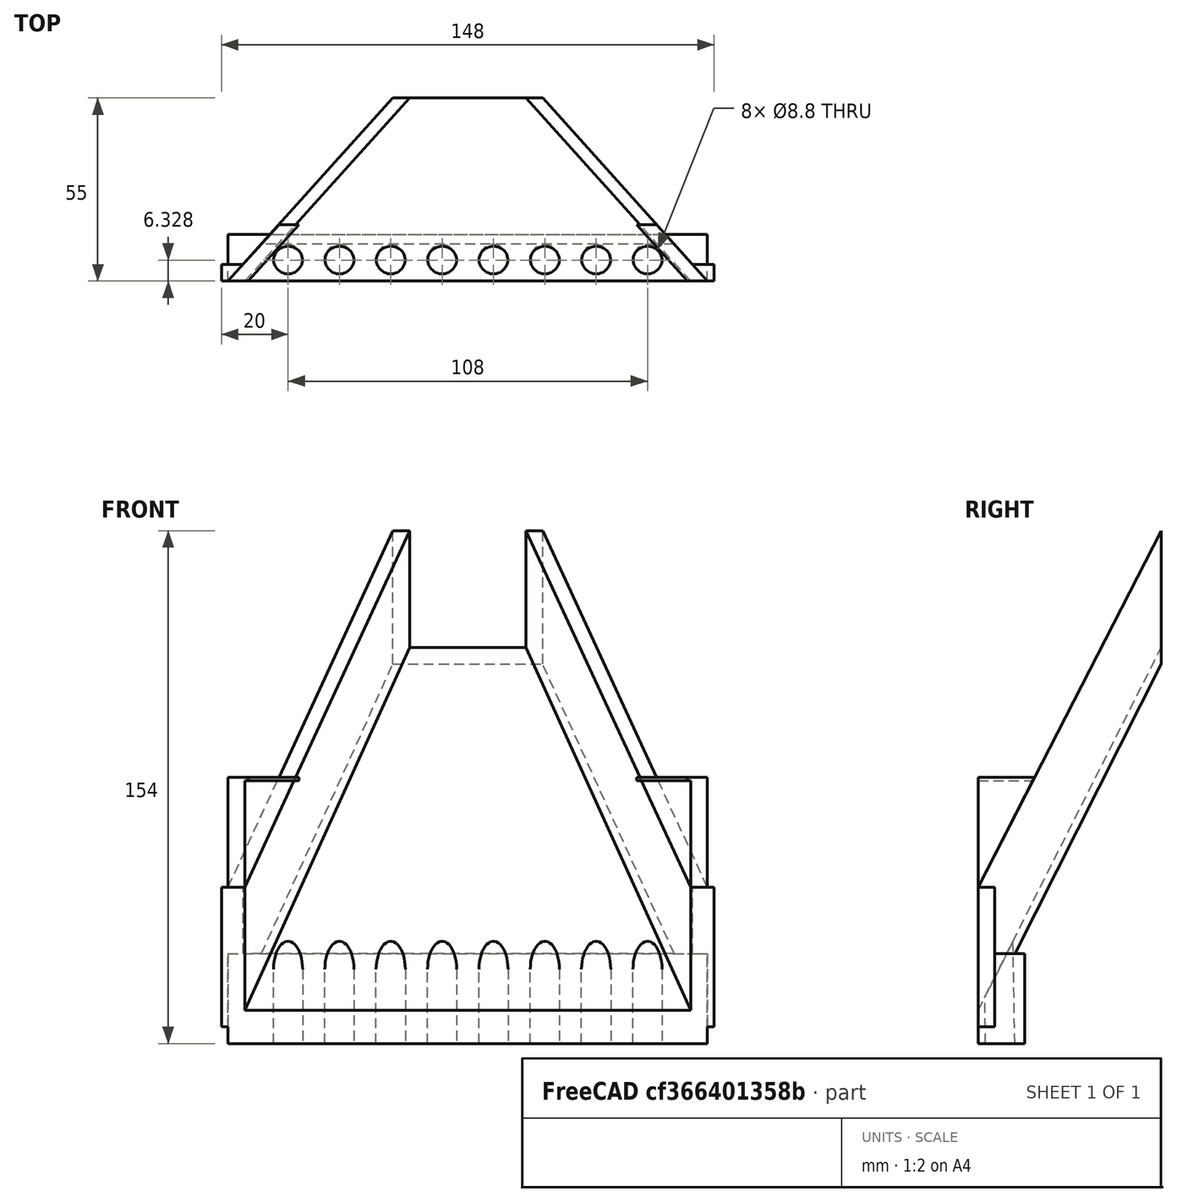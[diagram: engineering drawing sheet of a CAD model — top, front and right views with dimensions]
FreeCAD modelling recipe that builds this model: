
FCSTD DOCUMENT  (FreeCAD 0.20R29603 (Git))
Label: trichter_Ausgang4
License: All rights reserved
LicenseURL: http://en.wikipedia.org/wiki/All_rights_reserved
objects: TechDraw::DrawViewDimension×24, TechDraw::DrawProjGroupItem×9, PartDesign::AdditiveWedge×5, PartDesign::Body×3, TechDraw::DrawSVGTemplate×2, PartDesign::AdditiveBox×2, TechDraw::DrawPage×2, TechDraw::DrawProjGroup×2, PartDesign::SubtractiveWedge×1, PartDesign::SubtractiveCylinder×1, PartDesign::LinearPattern×1, TechDraw::DrawViewDetail×1
note: 22 computed .brp shape members not serialized (recipe doc carries the construction recipe); baked Part::Feature solids carry a one-line shape summary decoded from their .brp

FEATURE [TechDraw::DrawSVGTemplate] Template001
  EditableTexts = Designed_by_Name=B.Schulze; Drawing_number=1; FC-Date=11.08.2023; FC-SC=Scale; FC-SH=6; FC-Title=Eisdosierer; Subtitle=Trichter Ausgang
  Height = 210
  Orientation = 1
  Width = 297
FEATURE [TechDraw::DrawSVGTemplate] Template
  EditableTexts = Designed_by_Name=B. Schulze; Drawing_number=1; FC-Date=13.09.2023; FC-SC=1:1; FC-SH=7; FC-Title=Eisdosierer; Subtitle=Trichter Ausgang Seiten
  Height = 210
  Orientation = 1
  Width = 297
FEATURE [PartDesign::Body] Body
  Group = -> [Wedge,Box,Box001,Wedge001,Cylinder,LinearPattern]
  Origin = -> Origin
  Tip = -> LinearPattern
FEATURE [PartDesign::AdditiveWedge] Wedge
  AttacherType = Attacher::AttachEngine3D
  MapMode = 2
  Support = -> [Body]
  X2max = 94.5
  X2min = 49.5
  Xmax = 144
  Xmin = 0
  Ymax = 55
  Ymin = 0
  Z2max = 149
  Z2min = 109
  Zmax = 42
  Zmin = 0
FEATURE [PartDesign::AdditiveBox] Box
  AttacherType = Attacher::AttachEngine3D
  AttachmentOffset = pos=(-2,0,0) rot=(0,0,1;0rad)
  BaseFeature = -> Wedge
  Height = 42
  Length = 148
  MapMode = 2
  Placement = pos=(-2,0,0) rot=(0,0,1;0rad)
  Support = -> [Body]
  Width = 5
FEATURE [PartDesign::AdditiveBox] Box001
  AttacherType = Attacher::AttachEngine3D
  AttachmentOffset = pos=(0,0,-5) rot=(0,0,1;0rad)
  BaseFeature = -> Box
  Height = 27
  Length = 144
  MapMode = 2
  Placement = pos=(0,0,-5) rot=(0,0,1;0rad)
  Support = -> [Body]
  Width = 14
FEATURE [PartDesign::SubtractiveWedge] Wedge001
  AttacherType = Attacher::AttachEngine3D
  BaseFeature = -> Box001
  MapMode = 2
  Support = -> [Body]
  X2max = 89.5
  X2min = 54.5
  Xmax = 139
  Xmin = 5
  Ymax = 55
  Ymin = 0
  Z2max = 149
  Z2min = 114
  Zmax = 42
  Zmin = 5
FEATURE [PartDesign::SubtractiveCylinder] Cylinder
  Angle = 360
  AttacherType = Attacher::AttachEngine3D
  AttachmentOffset = pos=(18,-6,-34) rot=(1,0,0;0.017453rad)
  BaseFeature = -> Wedge001
  FirstAngle = 0
  Height = 35
  MapMode = 5
  Placement = pos=(18,6,29) rot=(1,0,0;3.15905rad)
  Radius = 4.4
  SecondAngle = 0
  Support = -> [Box001]
FEATURE [PartDesign::LinearPattern] LinearPattern
  BaseFeature = -> Cylinder
  Direction = -> X_Axis
  Length = 108
  Occurrences = 8
  Originals = -> [Cylinder]
  Placement = pos=(18,6,29) rot=(1,0,0;3.15905rad)
FEATURE [TechDraw::DrawPage] Page001
  KeepUpdated = true
  NextBalloonIndex = 1
  ProjectionType = 0
  Template = -> Template001
  Views = -> [ProjGroup,Detail,Dimension,Dimension001,Dimension002,Dimension003,Dimension004,Dimension005,Dimension006,Dimension007,Dimension008,Dimension009,Dimension010,Dimension011,Dimension012,Dimension013,Dimension014,Dimension015]
FEATURE [TechDraw::DrawProjGroup] ProjGroup
  Anchor = -> ProjItem
  AutoDistribute = false
  LockPosition = false
  ProjectionType = 0
  Rotation = 0
  Scale = 0.333333
  ScaleType = 2
  Source = -> [Body]
  Views = -> [ProjItem,ProjItem001,ProjItem002,ProjItem003,ProjItem004,ProjItem005,ProjItem006]
  X = 116.869
  Y = 105.822
  spacingX = 15
  spacingY = 15
FEATURE [TechDraw::DrawProjGroupItem] ProjItem  label="Front"
  CoarseView = false
  Direction = (-3e-16,0,1)
  Focus = 100
  HardHidden = false
  IsoCount = 0
  IsoHidden = false
  IsoVisible = false
  LockPosition = true
  Perspective = false
  Rotation = 0
  RotationVector = (0,0,1)
  Scale = 0.333333
  ScaleType = 2
  SeamHidden = false
  SeamVisible = true
  SmoothHidden = false
  SmoothVisible = true
  Source = -> [Body]
  Type = 0
  X = 0
  XDirection = (-1,0,-3e-16)
  Y = 0
FEATURE [TechDraw::DrawProjGroupItem] ProjItem001  label="Bottom"
  CoarseView = false
  Direction = (0,1,0)
  Focus = 100
  HardHidden = false
  IsoCount = 0
  IsoHidden = false
  IsoVisible = false
  LockPosition = false
  Perspective = false
  Rotation = 0
  RotationVector = (1,0,0)
  Scale = 0.333333
  ScaleType = 2
  SeamHidden = false
  SeamVisible = true
  SmoothHidden = false
  SmoothVisible = true
  Source = -> [Body]
  Type = 5
  X = 0
  XDirection = (-1,0,-3e-16)
  Y = 55.5717
FEATURE [TechDraw::DrawProjGroupItem] ProjItem002  label="FrontBottomLeft"
  CoarseView = false
  Direction = (0.57735,0.57735,0.57735)
  Focus = 100
  HardHidden = false
  IsoCount = 0
  IsoHidden = false
  IsoVisible = false
  LockPosition = false
  Perspective = false
  Rotation = 0
  RotationVector = (1,0,0)
  Scale = 0.333333
  ScaleType = 2
  SeamHidden = false
  SeamVisible = true
  SmoothHidden = false
  SmoothVisible = true
  Source = -> [Body]
  Type = 8
  X = 71.7719
  XDirection = (-0.707107,0,0.707107)
  Y = 57.8217
FEATURE [TechDraw::DrawProjGroupItem] ProjItem003  label="Top"
  CoarseView = false
  Direction = (0,-1,0)
  Focus = 100
  HardHidden = false
  IsoCount = 0
  IsoHidden = false
  IsoVisible = false
  LockPosition = false
  Perspective = false
  Rotation = 0
  RotationVector = (1,0,0)
  Scale = 0.333333
  ScaleType = 2
  SeamHidden = false
  SeamVisible = true
  SmoothHidden = false
  SmoothVisible = true
  Source = -> [Body]
  Type = 4
  X = 0
  XDirection = (-1,0,-3e-16)
  Y = -60.5218
FEATURE [TechDraw::DrawProjGroupItem] ProjItem004  label="Left"
  CoarseView = false
  Direction = (1,0,4e-16)
  Focus = 100
  HardHidden = false
  IsoCount = 0
  IsoHidden = false
  IsoVisible = false
  LockPosition = false
  Perspective = false
  Rotation = 0
  RotationVector = (1,0,0)
  Scale = 0.333333
  ScaleType = 2
  SeamHidden = false
  SeamVisible = true
  SmoothHidden = false
  SmoothVisible = true
  Source = -> [Body]
  Type = 1
  X = 73.572
  XDirection = (-4e-16,0,1)
  Y = 0
FEATURE [TechDraw::DrawProjGroupItem] ProjItem005  label="Right"
  CoarseView = false
  Direction = (-1,0,-2e-16)
  Focus = 100
  HardHidden = false
  IsoCount = 0
  IsoHidden = false
  IsoVisible = false
  LockPosition = false
  Perspective = false
  Rotation = 0
  RotationVector = (1,0,0)
  Scale = 0.333333
  ScaleType = 2
  SeamHidden = false
  SeamVisible = true
  SmoothHidden = false
  SmoothVisible = true
  Source = -> [Body]
  Type = 2
  X = -73.572
  XDirection = (2e-16,0,-1)
  Y = 0
FEATURE [TechDraw::DrawProjGroupItem] ProjItem006  label="Rear"
  CoarseView = false
  Direction = (3e-16,0,-1)
  Focus = 100
  HardHidden = false
  IsoCount = 0
  IsoHidden = false
  IsoVisible = false
  LockPosition = false
  Perspective = false
  Rotation = 0
  RotationVector = (1,0,0)
  Scale = 0.333333
  ScaleType = 2
  SeamHidden = false
  SeamVisible = true
  SmoothHidden = false
  SmoothVisible = true
  Source = -> [Body]
  Type = 3
  X = 135.894
  XDirection = (1,0,3e-16)
  Y = 0
FEATURE [TechDraw::DrawViewDetail] Detail
  AnchorPoint = (-53.15,20.74,0)
  BaseView = -> ProjItem006
  Caption = Schlauchbohrung
  CoarseView = false
  Direction = (3e-16,0,-1)
  Focus = 100
  HardHidden = false
  IsoCount = 0
  IsoHidden = false
  IsoVisible = false
  LockPosition = false
  Perspective = false
  Radius = 6
  Reference = 1
  Rotation = 0
  Scale = 2
  ScaleType = 2
  SeamHidden = false
  SeamVisible = true
  SmoothHidden = false
  SmoothVisible = true
  Source = -> [Body]
  X = 245.614
  XDirection = (1,0,3e-16)
  Y = 175.252
FEATURE [TechDraw::DrawViewDimension] Dimension
  AngleOverride = false
  Arbitrary = false
  ArbitraryTolerances = false
  EqualTolerance = true
  ExtensionAngle = 0
  FormatSpec = %.2w
  FormatSpecOverTolerance = %+.2w
  FormatSpecUnderTolerance = %+.2w
  Inverted = false
  LineAngle = 0
  LockPosition = false
  MeasureType = 1
  OverTolerance = 0
  References2D = -> [Detail]
  Rotation = 0
  ScaleType = 0
  TheoreticalExact = false
  Type = 1
  UnderTolerance = 0
  X = -0.438518
  Y = 22.5625
FEATURE [TechDraw::DrawViewDimension] Dimension001
  AngleOverride = false
  Arbitrary = false
  ArbitraryTolerances = false
  EqualTolerance = true
  ExtensionAngle = 0
  FormatSpec = %.2w
  FormatSpecOverTolerance = %+.2w
  FormatSpecUnderTolerance = %+.2w
  Inverted = false
  LineAngle = 0
  LockPosition = false
  MeasureType = 1
  OverTolerance = 0
  References2D = -> [ProjItem001]
  Rotation = 0
  ScaleType = 0
  TheoreticalExact = false
  Type = 1
  UnderTolerance = 0
  X = -1.3369
  Y = 36.2931
FEATURE [TechDraw::DrawViewDimension] Dimension002
  AngleOverride = false
  Arbitrary = false
  ArbitraryTolerances = false
  EqualTolerance = true
  ExtensionAngle = 0
  FormatSpec = %.2w
  FormatSpecOverTolerance = %+.2w
  FormatSpecUnderTolerance = %+.2w
  Inverted = false
  LineAngle = 0
  LockPosition = false
  MeasureType = 1
  OverTolerance = 0
  References2D = -> [ProjItem001]
  Rotation = 0
  ScaleType = 0
  TheoreticalExact = false
  Type = 1
  UnderTolerance = 0
  X = 0.121131
  Y = 22.0827
FEATURE [TechDraw::DrawViewDimension] Dimension003
  AngleOverride = false
  Arbitrary = false
  ArbitraryTolerances = false
  EqualTolerance = true
  ExtensionAngle = 0
  FormatSpec = %.2w
  FormatSpecOverTolerance = %+.2w
  FormatSpecUnderTolerance = %+.2w
  Inverted = false
  LineAngle = 0
  LockPosition = false
  MeasureType = 1
  OverTolerance = 0
  References2D = -> [ProjItem001]
  Rotation = 0
  ScaleType = 0
  TheoreticalExact = false
  Type = 2
  UnderTolerance = 0
  X = -23.8213
  Y = 22.4046
FEATURE [TechDraw::DrawViewDimension] Dimension004
  AngleOverride = false
  Arbitrary = false
  ArbitraryTolerances = false
  EqualTolerance = true
  ExtensionAngle = 0
  FormatSpec = %.2w
  FormatSpecOverTolerance = %+.2w
  FormatSpecUnderTolerance = %+.2w
  Inverted = false
  LineAngle = 0
  LockPosition = false
  MeasureType = 1
  OverTolerance = 0
  References2D = -> [ProjItem001]
  Rotation = 0
  ScaleType = 0
  TheoreticalExact = false
  Type = 2
  UnderTolerance = 0
  X = 20.0194
  Y = 19.9974
FEATURE [TechDraw::DrawViewDimension] Dimension005
  AngleOverride = false
  Arbitrary = false
  ArbitraryTolerances = false
  EqualTolerance = true
  ExtensionAngle = 0
  FormatSpec = %.2w
  FormatSpecOverTolerance = %+.2w
  FormatSpecUnderTolerance = %+.2w
  Inverted = false
  LineAngle = 0
  LockPosition = false
  MeasureType = 1
  OverTolerance = 0
  References2D = -> [ProjItem004]
  Rotation = 0
  ScaleType = 0
  TheoreticalExact = false
  Type = 1
  UnderTolerance = 0
  X = -21.4466
  Y = -3.72737
FEATURE [TechDraw::DrawViewDimension] Dimension006
  AngleOverride = false
  Arbitrary = false
  ArbitraryTolerances = false
  EqualTolerance = true
  ExtensionAngle = 0
  FormatSpec = %.2w
  FormatSpecOverTolerance = %+.2w
  FormatSpecUnderTolerance = %+.2w
  Inverted = false
  LineAngle = 0
  LockPosition = false
  MeasureType = 1
  OverTolerance = 0
  References2D = -> [ProjItem004]
  Rotation = 0
  ScaleType = 0
  TheoreticalExact = false
  Type = 0
  UnderTolerance = 0
  X = -2.59202
  Y = -2.62069
FEATURE [TechDraw::DrawViewDimension] Dimension007
  AngleOverride = false
  Arbitrary = false
  ArbitraryTolerances = false
  EqualTolerance = true
  ExtensionAngle = 0
  FormatSpec = %.2w
  FormatSpecOverTolerance = %+.2w
  FormatSpecUnderTolerance = %+.2w
  Inverted = false
  LineAngle = 0
  LockPosition = false
  MeasureType = 1
  OverTolerance = 0
  References2D = -> [ProjItem004]
  Rotation = 0
  ScaleType = 0
  TheoreticalExact = false
  Type = 0
  UnderTolerance = 0
  X = 14.6032
  Y = 9.18643
FEATURE [TechDraw::DrawViewDimension] Dimension008
  AngleOverride = false
  Arbitrary = false
  ArbitraryTolerances = false
  EqualTolerance = true
  ExtensionAngle = 0
  FormatSpec = %.2w
  FormatSpecOverTolerance = %+.2w
  FormatSpecUnderTolerance = %+.2w
  Inverted = false
  LineAngle = 0
  LockPosition = false
  MeasureType = 1
  OverTolerance = 0
  References2D = -> [ProjItem004]
  Rotation = 0
  ScaleType = 0
  TheoreticalExact = false
  Type = 2
  UnderTolerance = 0
  X = -37.081
  Y = 9.24611
FEATURE [TechDraw::DrawViewDimension] Dimension009
  AngleOverride = false
  Arbitrary = false
  ArbitraryTolerances = false
  EqualTolerance = true
  ExtensionAngle = 0
  FormatSpec = %.2w
  FormatSpecOverTolerance = %+.2w
  FormatSpecUnderTolerance = %+.2w
  Inverted = false
  LineAngle = 0
  LockPosition = false
  MeasureType = 1
  OverTolerance = 0
  References2D = -> [ProjItem004]
  Rotation = 0
  ScaleType = 0
  TheoreticalExact = false
  Type = 1
  UnderTolerance = 0
  X = -16.3864
  Y = 21.9147
FEATURE [TechDraw::DrawViewDimension] Dimension010
  AngleOverride = false
  Arbitrary = false
  ArbitraryTolerances = false
  EqualTolerance = true
  ExtensionAngle = 0
  FormatSpec = %.2w
  FormatSpecOverTolerance = %+.2w
  FormatSpecUnderTolerance = %+.2w
  Inverted = false
  LineAngle = 0
  LockPosition = false
  MeasureType = 1
  OverTolerance = 0
  References2D = -> [ProjItem005]
  Rotation = 0
  ScaleType = 0
  TheoreticalExact = false
  Type = 2
  UnderTolerance = 0
  X = -1.01314
  Y = 11.2756
FEATURE [TechDraw::DrawViewDimension] Dimension011
  AngleOverride = false
  Arbitrary = false
  ArbitraryTolerances = false
  EqualTolerance = true
  ExtensionAngle = 0
  FormatSpec = %.2w
  FormatSpecOverTolerance = %+.2w
  FormatSpecUnderTolerance = %+.2w
  Inverted = false
  LineAngle = 0
  LockPosition = false
  MeasureType = 1
  OverTolerance = 0
  References2D = -> [ProjItem003]
  Rotation = 0
  ScaleType = 0
  TheoreticalExact = false
  Type = 1
  UnderTolerance = 0
  X = 0.229292
  Y = 39.3296
FEATURE [TechDraw::DrawViewDimension] Dimension012
  AngleOverride = false
  Arbitrary = false
  ArbitraryTolerances = false
  EqualTolerance = true
  ExtensionAngle = 0
  FormatSpec = %.2w
  FormatSpecOverTolerance = %+.2w
  FormatSpecUnderTolerance = %+.2w
  Inverted = false
  LineAngle = 0
  LockPosition = false
  MeasureType = 1
  OverTolerance = 0
  References2D = -> [ProjItem003]
  Rotation = 0
  ScaleType = 0
  TheoreticalExact = false
  Type = 1
  UnderTolerance = 0
  X = -32.0146
  Y = 2.51505
FEATURE [TechDraw::DrawViewDimension] Dimension013
  AngleOverride = false
  Arbitrary = false
  ArbitraryTolerances = false
  EqualTolerance = true
  ExtensionAngle = 0
  FormatSpec = %.2w
  FormatSpecOverTolerance = %+.2w
  FormatSpecUnderTolerance = %+.2w
  Inverted = false
  LineAngle = 0
  LockPosition = false
  MeasureType = 1
  OverTolerance = 0
  References2D = -> [ProjItem003]
  Rotation = 0
  ScaleType = 0
  TheoreticalExact = false
  Type = 2
  UnderTolerance = 0
  X = 30.6495
  Y = 29.6155
FEATURE [TechDraw::DrawViewDimension] Dimension014
  AngleOverride = false
  Arbitrary = false
  ArbitraryTolerances = false
  EqualTolerance = true
  ExtensionAngle = 0
  FormatSpec = %.2w
  FormatSpecOverTolerance = %+.2w
  FormatSpecUnderTolerance = %+.2w
  Inverted = false
  LineAngle = 0
  LockPosition = false
  MeasureType = 1
  OverTolerance = 0
  References2D = -> [ProjItem006]
  Rotation = 0
  ScaleType = 0
  TheoreticalExact = false
  Type = 1
  UnderTolerance = 0
  X = -29.2699
  Y = 19.6135
FEATURE [TechDraw::DrawViewDimension] Dimension015
  AngleOverride = false
  Arbitrary = false
  ArbitraryTolerances = false
  EqualTolerance = true
  ExtensionAngle = 0
  FormatSpec = %.2w
  FormatSpecOverTolerance = %+.2w
  FormatSpecUnderTolerance = %+.2w
  Inverted = false
  LineAngle = 0
  LockPosition = false
  MeasureType = 1
  OverTolerance = 0
  References2D = -> [ProjItem006]
  Rotation = 0
  ScaleType = 0
  TheoreticalExact = false
  Type = 1
  UnderTolerance = 0
  X = 0.949326
  Y = 16.3942
FEATURE [PartDesign::Body] Body001  label="Seite1"
  Group = -> [Wedge002,Wedge005]
  Origin = -> Origin001
  Tip = -> Wedge005
FEATURE [PartDesign::AdditiveWedge] Wedge002
  AttacherType = Attacher::AttachEngine3D
  AttachmentOffset = pos=(0,0,42) rot=(0,0,1;0rad)
  MapMode = 2
  Placement = pos=(0,0,42) rot=(0,0,1;0rad)
  Support = -> [Body]
  X2max = 20.27
  X2min = 15.27
  Xmax = 5
  Xmin = 0
  Ymax = 16.96
  Ymin = 0
  Z2max = 33
  Z2min = 33
  Zmax = 33
  Zmin = 0
FEATURE [PartDesign::Body] Body002  label="Seite2"
  Group = -> [Wedge003,Wedge004]
  Origin = -> Origin002
  Tip = -> Wedge004
FEATURE [PartDesign::AdditiveWedge] Wedge003
  AttacherType = Attacher::AttachEngine3D
  AttachmentOffset = pos=(123.73,0,42) rot=(0,0,1;0rad)
  MapMode = 2
  Placement = pos=(123.73,0,42) rot=(0,0,1;0rad)
  Support = -> [Body]
  X2max = 5
  X2min = 0
  Xmax = 20.27
  Xmin = 15.27
  Ymax = 16.96
  Ymin = 0
  Z2max = 33
  Z2min = 33
  Zmax = 33
  Zmin = 0
FEATURE [PartDesign::AdditiveWedge] Wedge004
  AttacherType = Attacher::AttachEngine3D
  AttachmentOffset = pos=(122.73,0,74) rot=(0,0,1;0rad)
  BaseFeature = -> Wedge003
  MapMode = 2
  Placement = pos=(122.73,0,74) rot=(0,0,1;0rad)
  Support = -> [Body]
  X2max = 1
  X2min = 0
  Xmax = 16.27
  Xmin = 15.27
  Ymax = 16.96
  Ymin = 0
  Z2max = 1
  Z2min = 0
  Zmax = 1
  Zmin = 0
FEATURE [PartDesign::AdditiveWedge] Wedge005
  AttacherType = Attacher::AttachEngine3D
  AttachmentOffset = pos=(5,0,74) rot=(0,0,1;0rad)
  BaseFeature = -> Wedge002
  MapMode = 2
  Placement = pos=(5,0,74) rot=(0,0,1;0rad)
  Support = -> [Body]
  X2max = 16.27
  X2min = 15.27
  Xmax = 1
  Xmin = 0
  Ymax = 16.96
  Ymin = 0
  Z2max = 1
  Z2min = 0
  Zmax = 1
  Zmin = 0
FEATURE [TechDraw::DrawPage] Page
  KeepUpdated = true
  NextBalloonIndex = 1
  ProjectionType = 0
  Template = -> Template
  Views = -> [ProjGroup001,Dimension016,Dimension017,Dimension018,Dimension019,Dimension020,Dimension021,Dimension022,Dimension023]
FEATURE [TechDraw::DrawProjGroup] ProjGroup001
  Anchor = -> ProjItem007
  AutoDistribute = true
  LockPosition = false
  ProjectionType = 0
  Rotation = 0
  ScaleType = 0
  Source = -> [Body002]
  Views = -> [ProjItem007,ProjItem009]
  X = 62.6533
  Y = 151.174
  spacingX = 15
  spacingY = 15
FEATURE [TechDraw::DrawProjGroupItem] ProjItem007  label="Front001"
  CoarseView = false
  Direction = (0,-1,0)
  Focus = 100
  HardHidden = false
  IsoCount = 0
  IsoHidden = false
  IsoVisible = false
  LockPosition = true
  Perspective = false
  Rotation = 0
  RotationVector = (-1,0,0)
  ScaleType = 2
  SeamHidden = false
  SeamVisible = true
  SmoothHidden = false
  SmoothVisible = true
  Source = -> [Body002]
  Type = 0
  X = 0
  XDirection = (3e-16,0,1)
  Y = 0
FEATURE [TechDraw::DrawViewDimension] Dimension016
  AngleOverride = false
  Arbitrary = false
  ArbitraryTolerances = false
  EqualTolerance = true
  ExtensionAngle = 0
  FormatSpec = %.2w
  FormatSpecOverTolerance = %+.2w
  FormatSpecUnderTolerance = %+.2w
  Inverted = false
  LineAngle = 0
  LockPosition = false
  MeasureType = 1
  OverTolerance = 0
  References2D = -> [ProjItem007]
  Rotation = 0
  ScaleType = 0
  TheoreticalExact = false
  Type = 1
  UnderTolerance = 0
  X = 4.32374
  Y = -28.1814
FEATURE [TechDraw::DrawViewDimension] Dimension017
  AngleOverride = false
  Arbitrary = false
  ArbitraryTolerances = false
  EqualTolerance = true
  ExtensionAngle = 0
  FormatSpec = %.2w
  FormatSpecOverTolerance = %+.2w
  FormatSpecUnderTolerance = %+.2w
  Inverted = false
  LineAngle = 0
  LockPosition = false
  MeasureType = 1
  OverTolerance = 0
  References2D = -> [ProjItem007]
  Rotation = 0
  ScaleType = 0
  TheoreticalExact = false
  Type = 0
  UnderTolerance = 0
  X = -9.87309
  Y = 16.3095
FEATURE [TechDraw::DrawViewDimension] Dimension018
  AngleOverride = false
  Arbitrary = false
  ArbitraryTolerances = false
  EqualTolerance = true
  ExtensionAngle = 0
  FormatSpec = %.2w
  FormatSpecOverTolerance = %+.2w
  FormatSpecUnderTolerance = %+.2w
  Inverted = false
  LineAngle = 0
  LockPosition = false
  MeasureType = 1
  OverTolerance = 0
  References2D = -> [ProjItem007]
  Rotation = 0
  ScaleType = 0
  TheoreticalExact = false
  Type = 2
  UnderTolerance = 0
  X = -31.1364
  Y = -4.55349
FEATURE [TechDraw::DrawViewDimension] Dimension019
  AngleOverride = false
  Arbitrary = false
  ArbitraryTolerances = false
  EqualTolerance = true
  ExtensionAngle = 0
  FormatSpec = %.2w
  FormatSpecOverTolerance = %+.2w
  FormatSpecUnderTolerance = %+.2w
  Inverted = false
  LineAngle = 0
  LockPosition = false
  MeasureType = 1
  OverTolerance = 0
  References2D = -> [ProjItem007]
  Rotation = 0
  ScaleType = 0
  TheoreticalExact = false
  Type = 1
  UnderTolerance = 0
  X = 17.8689
  Y = 28.335
FEATURE [TechDraw::DrawViewDimension] Dimension020
  AngleOverride = false
  Arbitrary = false
  ArbitraryTolerances = false
  EqualTolerance = true
  ExtensionAngle = 0
  FormatSpec = %.2w
  FormatSpecOverTolerance = %+.2w
  FormatSpecUnderTolerance = %+.2w
  Inverted = false
  LineAngle = 0
  LockPosition = false
  MeasureType = 1
  OverTolerance = 0
  References2D = -> [ProjItem007]
  Rotation = 0
  ScaleType = 0
  TheoreticalExact = false
  Type = 2
  UnderTolerance = 0
  X = 23.2293
  Y = 4.26788
FEATURE [TechDraw::DrawViewDimension] Dimension021
  AngleOverride = false
  Arbitrary = false
  ArbitraryTolerances = false
  EqualTolerance = true
  ExtensionAngle = 0
  FormatSpec = %.2w
  FormatSpecOverTolerance = %+.2w
  FormatSpecUnderTolerance = %+.2w
  Inverted = false
  LineAngle = 0
  LockPosition = false
  MeasureType = 1
  OverTolerance = 0
  References2D = -> [ProjItem007]
  Rotation = 0
  ScaleType = 0
  TheoreticalExact = false
  Type = 2
  UnderTolerance = 0
  X = 28.916
  Y = -4.53058
FEATURE [TechDraw::DrawProjGroupItem] ProjItem009  label="Left001"
  CoarseView = false
  Direction = (-3e-16,-1e-16,-1)
  Focus = 100
  HardHidden = false
  IsoCount = 0
  IsoHidden = false
  IsoVisible = false
  LockPosition = false
  Perspective = false
  Rotation = 0
  RotationVector = (1,0,0)
  ScaleType = 2
  SeamHidden = false
  SeamVisible = true
  SmoothHidden = false
  SmoothVisible = true
  Source = -> [Body002]
  Type = 1
  X = 88.1786
  XDirection = (0,-1,1e-16)
  Y = 0
FEATURE [TechDraw::DrawViewDimension] Dimension022
  AngleOverride = false
  Arbitrary = false
  ArbitraryTolerances = false
  EqualTolerance = true
  ExtensionAngle = 0
  FormatSpec = %.2w
  FormatSpecOverTolerance = %+.2w
  FormatSpecUnderTolerance = %+.2w
  Inverted = false
  LineAngle = 0
  LockPosition = false
  MeasureType = 1
  OverTolerance = 0
  References2D = -> [ProjItem009]
  Rotation = 0
  ScaleType = 0
  TheoreticalExact = false
  Type = 6
  UnderTolerance = 0
  X = 4.46448
  Y = -5.08743
FEATURE [TechDraw::DrawViewDimension] Dimension023
  AngleOverride = false
  Arbitrary = false
  ArbitraryTolerances = false
  EqualTolerance = true
  ExtensionAngle = 0
  FormatSpec = %.2w
  FormatSpecOverTolerance = %+.2w
  FormatSpecUnderTolerance = %+.2w
  Inverted = false
  LineAngle = 0
  LockPosition = false
  MeasureType = 1
  OverTolerance = 0
  References2D = -> [ProjItem009]
  Rotation = 0
  ScaleType = 0
  TheoreticalExact = false
  Type = 6
  UnderTolerance = 0
  X = -5.3989
  Y = 6.95628
